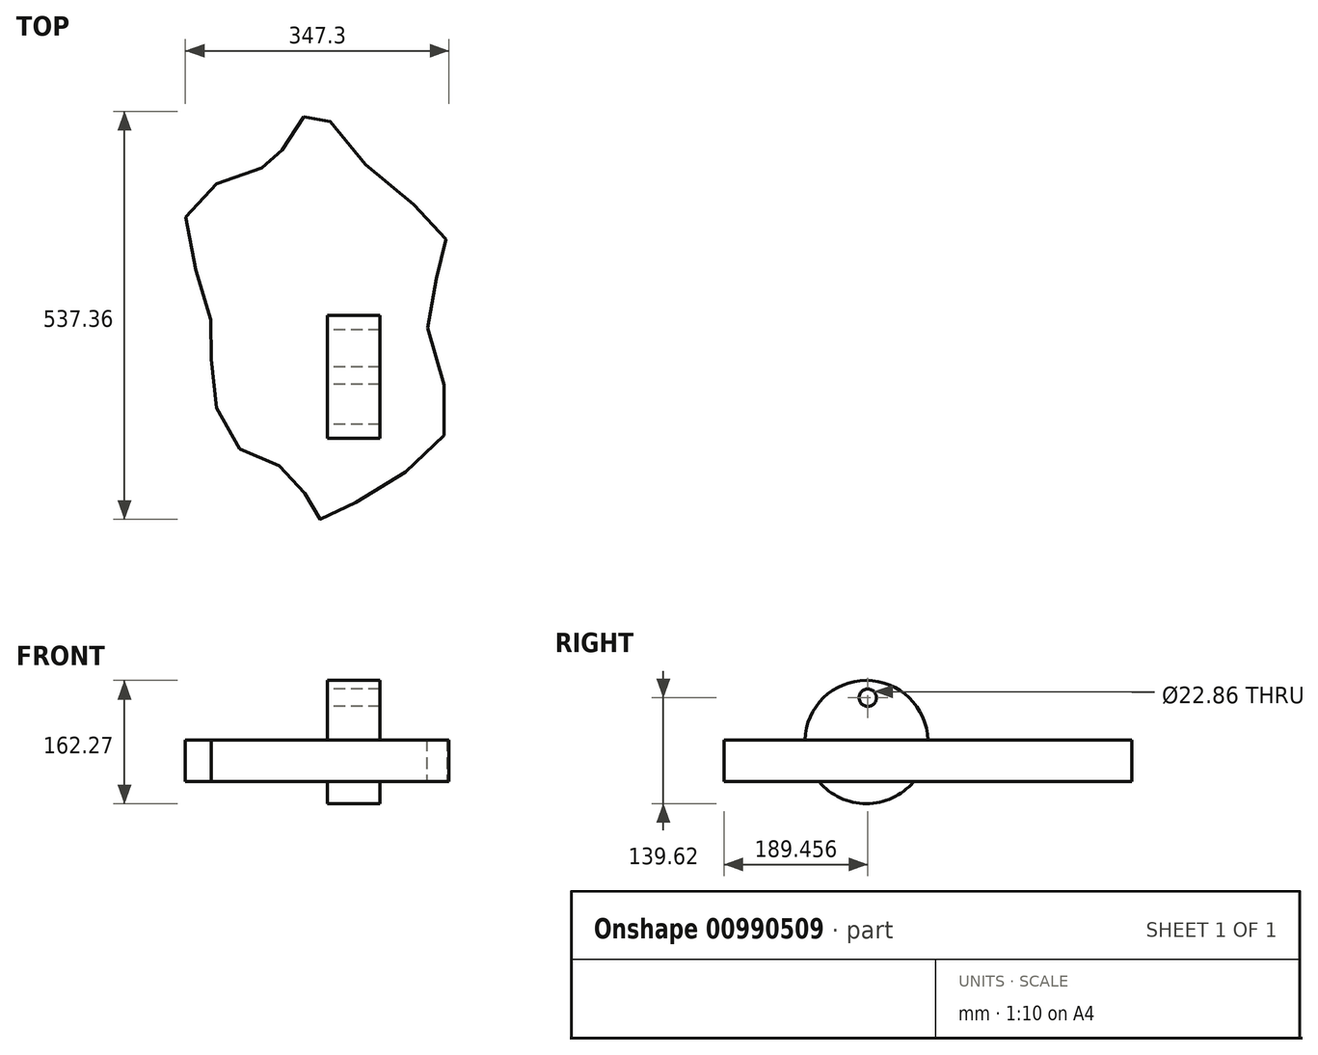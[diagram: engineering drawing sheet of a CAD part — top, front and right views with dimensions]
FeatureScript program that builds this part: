
annotation { "Feature Type Name" : "Feature", "Feature Type Description" : "" }
export const myFeature = defineFeature(function(context is Context, id is Id, definition is map)
    precondition{}
    {
        {
            var Q0;
            Q0=qCreatedBy(makeId("Right.planeOp"),FACE);
            var sketch = newSketch(context, id + "F0", { "sketchPlane" : qUnion([Q0])});
            skCircle(sketch, "E0", {"center": v(-85.64, 52.07) * mm, "radius": 81.13 * mm});
            skSolve(sketch);
        }
        {
            var Q0;
            Q0=makeQuery(id+"F0.imprint","IMPRINT",FACE,{"disambiguationData":[TD([[makeQuery(id+"F0.imprint","IMPRINT",EDGE,{"derivedFrom":sQuery(id+"F0.wireOp",EDGE,"E0")}),1.0]])]});
            extrude(context, id + "F1", {"entities" : qUnion([Q0]), "depth" : 69.34 * mm, "offsetDistance" : 25.4 * mm});
        }
        {
            var Q0;
            Q0=qCreatedBy(makeId("Top.planeOp"),FACE);
            var sketch = newSketch(context, id + "F2", { "sketchPlane" : qUnion([Q0])});
            skFitSpline(sketch, "E1", {"points": [v(-86.44, 189.41) * mm, v(-182.03, 139.59) * mm, v(-157.55, 9) * mm, v(-152.98, -74.12) * mm, v(-116.7, -179.67) * mm, v(-42.15, -215.95) * mm, v(-15.13, -271.1) * mm, v(54.17, -240.74) * mm, v(158.84, -148.16) * mm, v(131.3, 0) * mm, v(156.84, 92.96) * mm, v(53.23, 190.73) * mm, v(-18.55, 264) * mm, v(-59.6, 213.49) * mm, v(-86.44, 189.41) * mm]});
            skSolve(sketch);
        }
        {
            var Q0;
            Q0=makeQuery(id+"F2.imprint","IMPRINT",FACE,{"disambiguationData":[TD([[makeQuery(id+"F2.imprint","IMPRINT",EDGE,{"derivedFrom":sQuery(id+"F2.wireOp",EDGE,"E1")}),1.0]])]});
            extrude(context, id + "F3", {"entities" : qUnion([Q0]), "operationType" : NewBodyOperationType.ADD, "depth" : 54.86 * mm, "offsetDistance" : 25.4 * mm});
        }
        {
            var Q0;
            {var subQ0=sQuery(id+"F0.wireOp",EDGE,"E0");Q0=makeQuery(id+"F3.boolean.opBoolean","SPLIT",FACE,{"disambiguationData":[TD([makeQuery(id+"F3.opExtrude","CAP_FACE",FACE,{"disambiguationData":[OSD([sQuery(id+"F2.wireOp",EDGE,"E1")])],"isStart":false})])],"derivedFrom":makeQuery(id+"F1.opExtrude","CAP_FACE",FACE,{"disambiguationData":[OSD([subQ0])],"isStart":true})});}
            var sketch = newSketch(context, id + "F4", { "sketchPlane" : qUnion([Q0])});
            skCircle(sketch, "E2", {"center": v(83.78, 110.55) * mm, "radius": 11.96 * mm});
            skSolve(sketch);
        }
        {
            var Q0;
            Q0=sQuery(id+"F4.wireOp",VERTEX,"E2.center");
            var Q1;
            Q1=makeQuery(id+"F1.opExtrude","SWEPT_BODY",BODY,{"disambiguationData":[OSD([sQuery(id+"F0.wireOp",EDGE,"E0")])]});
            hole(context, id + "F5", {"style" : HoleStyle.C_BORE, "endStyle" : HoleEndStyle.THROUGH, "holeDiameter" : 21.59 * mm, "cBoreDiameter" : 22.86 * mm, "cBoreDepth" : 209.55 * mm, "majorDiameter" : 6.35 * mm, "isTappedThrough" : true, "tappedDepth" : 12.7 * mm, "tapClearance" : 3, "startFromSketch" : true, "locations" : qUnion([Q0]), "scope" : qUnion([Q1])});
        }
    });
